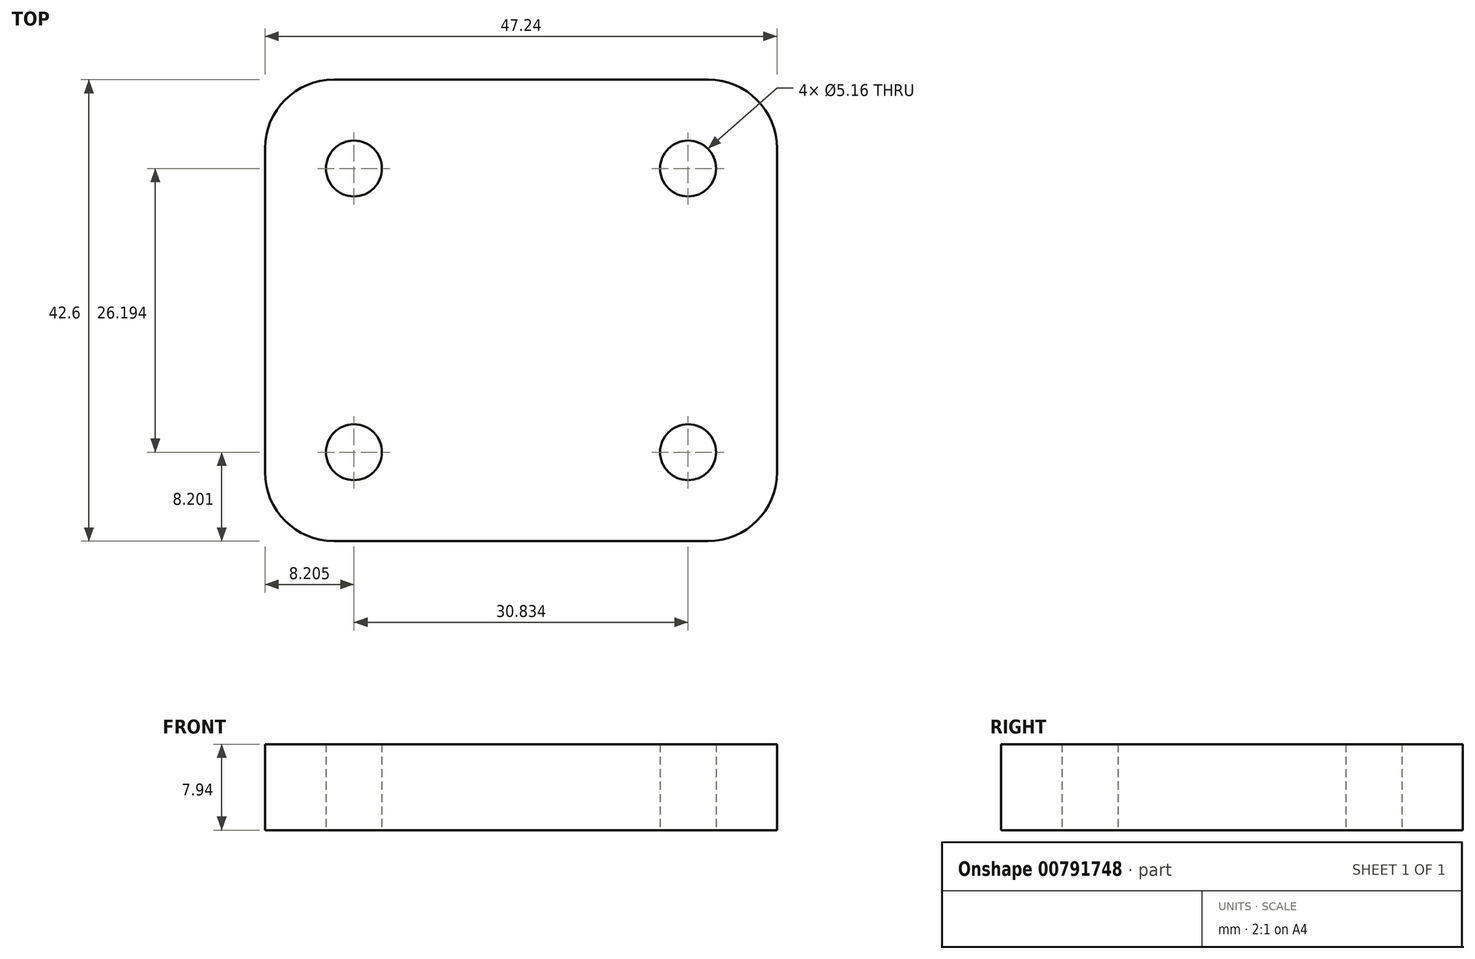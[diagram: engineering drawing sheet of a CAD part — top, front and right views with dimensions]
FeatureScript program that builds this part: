
annotation { "Feature Type Name" : "Feature", "Feature Type Description" : "" }
export const myFeature = defineFeature(function(context is Context, id is Id, definition is map)
    precondition{}
    {
        {
            var Q0;
            Q0=qCreatedBy(makeId("Top.planeOp"),FACE);
            var sketch = newSketch(context, id + "F0", { "sketchPlane" : qUnion([Q0])});
            skLineSegment(sketch, "E0.bottom", {"start": v(6.35, 0) * mm, "end": v(40.9, 0) * mm});
            skLineSegment(sketch, "E0.top", {"start": v(6.35, 42.6) * mm, "end": v(40.9, 42.6) * mm});
            skLineSegment(sketch, "E0.left", {"start": v(0, 6.35) * mm, "end": v(0, 36.25) * mm});
            skLineSegment(sketch, "E0.right", {"start": v(47.24, 6.35) * mm, "end": v(47.24, 36.25) * mm});
            skCircle(sketch, "E1", {"center": v(8.2, 8.2) * mm, "radius": 2.58 * mm});
            skCircle(sketch, "E2.0.1.0", {"center": v(8.2, 34.4) * mm, "radius": 2.58 * mm});
            skCircle(sketch, "E2.1.0.0", {"center": v(39.04, 8.2) * mm, "radius": 2.58 * mm});
            skCircle(sketch, "E2.1.1.0", {"center": v(39.04, 34.4) * mm, "radius": 2.58 * mm});
            skLineSegment(sketch, "E2.direction1", {"start": v(8.2, 8.2) * mm, "end": v(39.04, 8.2) * mm, "construction": true});
            skLineSegment(sketch, "E2.direction2", {"start": v(8.2, 8.2) * mm, "end": v(8.2, 34.4) * mm, "construction": true});
            skPoint(sketch, "E3.visualSharp", {"position": v(47.24, 42.6) * mm});
            skArc(sketch, "E3.filletArc", {"start": v(47.24, 36.25) * mm, "mid": v(45.38, 40.74) * mm, "end": v(40.9, 42.6) * mm});
            skPoint(sketch, "E4.visualSharp", {"position": v(0, 42.6) * mm});
            skArc(sketch, "E4.filletArc", {"start": v(6.35, 42.6) * mm, "mid": v(1.86, 40.74) * mm, "end": v(0, 36.25) * mm});
            skPoint(sketch, "E5.visualSharp", {"position": v(47.24, 0) * mm});
            skArc(sketch, "E5.filletArc", {"start": v(40.9, 0) * mm, "mid": v(45.38, 1.86) * mm, "end": v(47.24, 6.35) * mm});
            skPoint(sketch, "E6.visualSharp", {"position": v(0, 0) * mm});
            skArc(sketch, "E6.filletArc", {"start": v(0, 6.35) * mm, "mid": v(1.86, 1.86) * mm, "end": v(6.35, 0) * mm});
            skSolve(sketch);
        }
        {
            var Q0;
            Q0=qSketchRegion(id+"F0",true);
            extrude(context, id + "F1", {"entities" : qUnion([Q0]), "depth" : 7.94 * mm, "offsetDistance" : 25.4 * mm});
        }
    });
